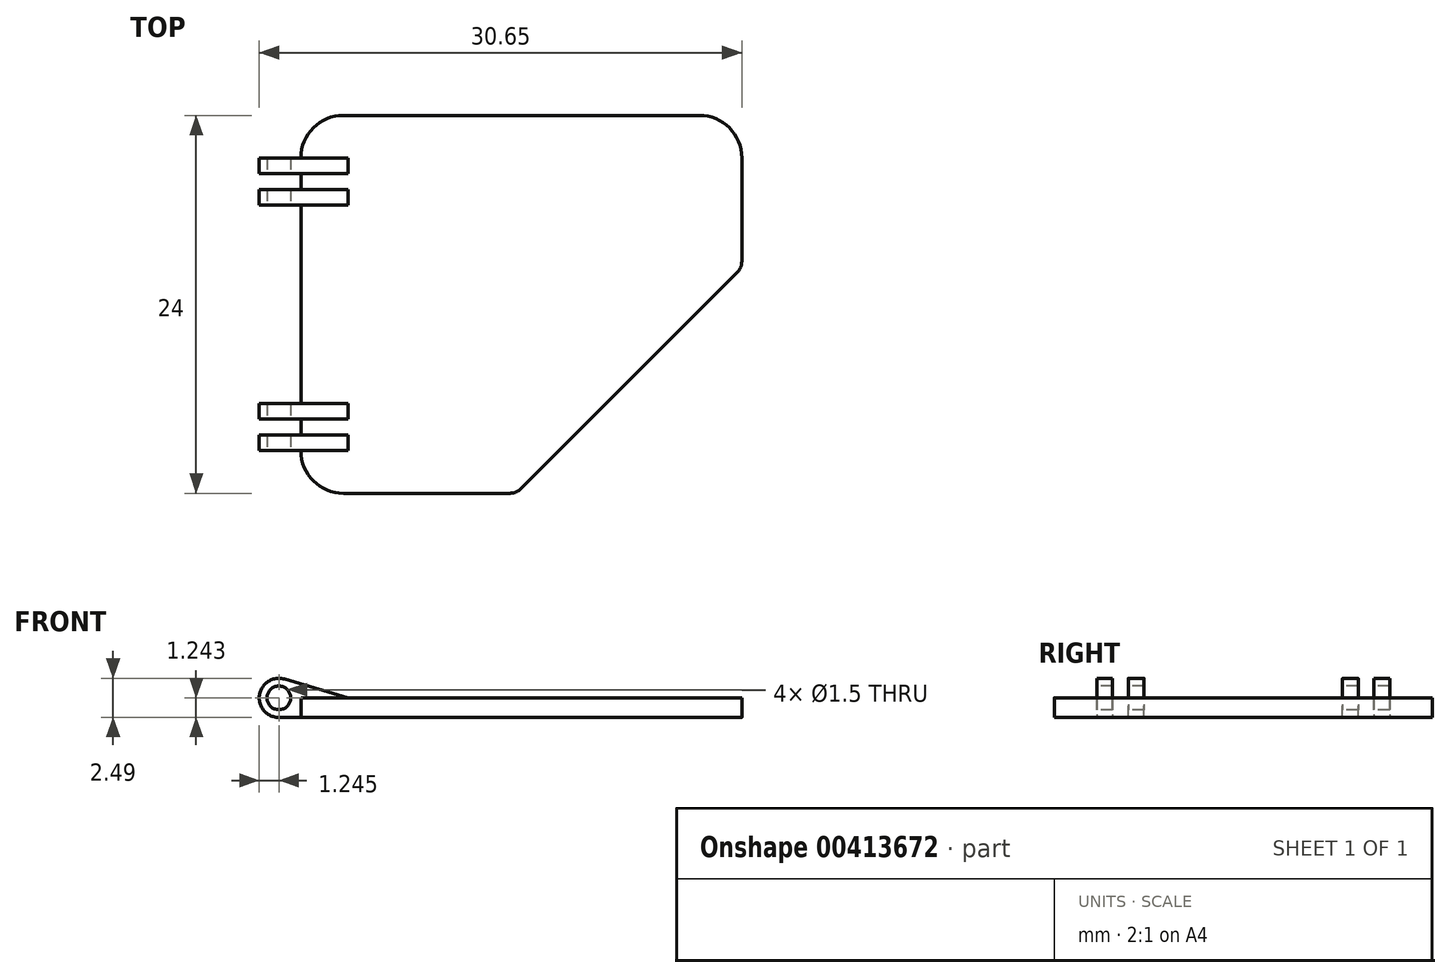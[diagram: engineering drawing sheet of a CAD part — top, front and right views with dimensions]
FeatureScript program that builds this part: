
annotation { "Feature Type Name" : "Feature", "Feature Type Description" : "" }
export const myFeature = defineFeature(function(context is Context, id is Id, definition is map)
    precondition{}
    {
        {
            var Q0;
            Q0=qCreatedBy(makeId("Top.planeOp"),FACE);
            var sketch = newSketch(context, id + "F0", { "sketchPlane" : qUnion([Q0])});
            skLineSegment(sketch, "E0", {"start": v(-10.68, 12.54) * mm, "end": v(-10.68, -6.06) * mm});
            skLineSegment(sketch, "E1", {"start": v(-7.98, -8.76) * mm, "end": v(2.6, -8.76) * mm});
            skLineSegment(sketch, "E2", {"start": v(3.3, -8.46) * mm, "end": v(17.02, 5.25) * mm});
            skLineSegment(sketch, "E3", {"start": v(17.32, 5.96) * mm, "end": v(17.32, 12.54) * mm});
            skLineSegment(sketch, "E4", {"start": v(14.62, 15.24) * mm, "end": v(-7.98, 15.24) * mm});
            skPoint(sketch, "E5.visualSharp", {"position": v(-10.68, 15.24) * mm});
            skArc(sketch, "E5.filletArc", {"start": v(-7.98, 15.24) * mm, "mid": v(-9.9, 14.45) * mm, "end": v(-10.68, 12.54) * mm});
            skPoint(sketch, "E6.visualSharp", {"position": v(-10.68, -8.76) * mm});
            skArc(sketch, "E6.filletArc", {"start": v(-10.68, -6.06) * mm, "mid": v(-9.9, -7.97) * mm, "end": v(-7.98, -8.76) * mm});
            skPoint(sketch, "E7.visualSharp", {"position": v(17.32, 15.24) * mm});
            skArc(sketch, "E7.filletArc", {"start": v(17.32, 12.54) * mm, "mid": v(16.52, 14.45) * mm, "end": v(14.62, 15.24) * mm});
            skPoint(sketch, "E8.visualSharp", {"position": v(3.02, -8.76) * mm});
            skArc(sketch, "E8.filletArc", {"start": v(2.6, -8.76) * mm, "mid": v(2.98, -8.68) * mm, "end": v(3.3, -8.46) * mm});
            skPoint(sketch, "E9.visualSharp", {"position": v(17.32, 5.54) * mm});
            skArc(sketch, "E9.filletArc", {"start": v(17.02, 5.25) * mm, "mid": v(17.24, 5.57) * mm, "end": v(17.32, 5.96) * mm});
            skSolve(sketch);
        }
        {
            var Q0;
            Q0 = qSketchRegion(id + "F0", true);
            extrude(context, id + "F1", {"entities" : qUnion([Q0]), "depth" : 1.25 * mm});
        }
        {
            var Q0;
            Q0=makeQuery(id+"F1.opExtrude","CAP_FACE",FACE,{"disambiguationData":[OSD([sQuery(id+"F0.wireOp",EDGE,"E0"),sQuery(id+"F0.wireOp",EDGE,"E1"),sQuery(id+"F0.wireOp",EDGE,"E2"),sQuery(id+"F0.wireOp",EDGE,"E3"),sQuery(id+"F0.wireOp",EDGE,"E4"),sQuery(id+"F0.wireOp",EDGE,"E5.filletArc"),sQuery(id+"F0.wireOp",EDGE,"E6.filletArc"),sQuery(id+"F0.wireOp",EDGE,"E7.filletArc"),sQuery(id+"F0.wireOp",EDGE,"E8.filletArc"),sQuery(id+"F0.wireOp",EDGE,"E9.filletArc")])],"isStart":false});
            var sketch = newSketch(context, id + "F2", { "sketchPlane" : qUnion([Q0])});
            skLineSegment(sketch, "E10", {"start": v(-10.68, 12.54) * mm, "end": v(-13.68, 12.54) * mm});
            skLineSegment(sketch, "E11", {"start": v(-13.68, 12.54) * mm, "end": v(-13.68, 11.54) * mm});
            skLineSegment(sketch, "E12", {"start": v(-13.68, 9.54) * mm, "end": v(-7.68, 9.54) * mm});
            skLineSegment(sketch, "E13", {"start": v(-7.68, 9.54) * mm, "end": v(-7.68, 10.54) * mm});
            skLineSegment(sketch, "E14", {"start": v(-7.68, 12.54) * mm, "end": v(-10.68, 12.54) * mm});
            skLineSegment(sketch, "E15", {"start": v(-10.68, -6.06) * mm, "end": v(-13.68, -6.06) * mm});
            skLineSegment(sketch, "E16", {"start": v(-13.68, -6.06) * mm, "end": v(-13.68, -5.06) * mm});
            skLineSegment(sketch, "E17", {"start": v(-13.68, -3.06) * mm, "end": v(-7.68, -3.06) * mm});
            skLineSegment(sketch, "E18", {"start": v(-7.68, -3.06) * mm, "end": v(-7.68, -4.06) * mm});
            skLineSegment(sketch, "E19", {"start": v(-7.68, -6.06) * mm, "end": v(-10.68, -6.06) * mm});
            skLineSegment(sketch, "E20.0", {"start": v(-10.68, 11.54) * mm, "end": v(-13.68, 11.54) * mm});
            skLineSegment(sketch, "E21.0", {"start": v(-7.68, 11.54) * mm, "end": v(-10.68, 11.54) * mm});
            skLineSegment(sketch, "E22.0", {"start": v(-13.68, 10.54) * mm, "end": v(-7.68, 10.54) * mm});
            skLineSegment(sketch, "E23.0", {"start": v(-13.68, -4.06) * mm, "end": v(-7.68, -4.06) * mm});
            skLineSegment(sketch, "E24.0", {"start": v(-10.68, -5.06) * mm, "end": v(-13.68, -5.06) * mm});
            skLineSegment(sketch, "E25.0", {"start": v(-7.68, -5.06) * mm, "end": v(-10.68, -5.06) * mm});
            skLineSegment(sketch, "E26.trimOffspring", {"start": v(-7.68, -5.06) * mm, "end": v(-7.68, -6.06) * mm});
            skLineSegment(sketch, "E27.trimOffspring", {"start": v(-13.68, -4.06) * mm, "end": v(-13.68, -3.06) * mm});
            skLineSegment(sketch, "E28.trimOffspring", {"start": v(-13.68, 10.54) * mm, "end": v(-13.68, 9.54) * mm});
            skLineSegment(sketch, "E29.trimOffspring", {"start": v(-7.68, 11.54) * mm, "end": v(-7.68, 12.54) * mm});
            skSolve(sketch);
        }
        {
            var Q0;
            Q0 = qSketchRegion(id + "F2", true);
            extrude(context, id + "F3", {"entities" : qUnion([Q0]), "operationType" : NewBodyOperationType.ADD, "endBound" : BoundingType.SYMMETRIC, "depth" : 5 * mm});
        }
        {
            var Q0;
            Q0=makeQuery(id+"F3.opExtrude","SWEPT_FACE",FACE,{"disambiguationData":[OSD([sQuery(id+"F2.wireOp",EDGE,"E15"),sQuery(id+"F2.wireOp",EDGE,"E19")])]});
            var sketch = newSketch(context, id + "F4", { "sketchPlane" : qUnion([Q0])});
            skLineSegment(sketch, "E30", {"start": v(-7.68, 1.25) * mm, "end": v(-7.68, 3.75) * mm});
            skLineSegment(sketch, "E31", {"start": v(-7.68, 3.75) * mm, "end": v(-13.68, 3.75) * mm});
            skLineSegment(sketch, "E32", {"start": v(-13.68, 3.75) * mm, "end": v(-13.68, -1.25) * mm});
            skLineSegment(sketch, "E33", {"start": v(-13.68, -1.25) * mm, "end": v(-7.68, -1.25) * mm});
            skLineSegment(sketch, "E34", {"start": v(-7.68, -1.25) * mm, "end": v(-7.68, 0) * mm});
            skLineSegment(sketch, "E35", {"start": v(-7.68, 0) * mm, "end": v(-10.68, 0) * mm});
            skPoint(sketch, "E36.centerSnap0", {"position": v(-10.68, 0.62) * mm});
            skLineSegment(sketch, "E37", {"start": v(-7.68, 1.25) * mm, "end": v(-10.68, 1.25) * mm});
            skLineSegment(sketch, "E38", {"start": v(-10.68, 1.25) * mm, "end": v(-10.68, 0) * mm});
            skPoint(sketch, "E39.11.internal.orphan", {"position": v(-7.68, 1.1) * mm});
            skPoint(sketch, "E40.center.orphan", {"position": v(-11.47, 0.62) * mm});
            skCircle(sketch, "E41", {"center": v(-12.08, 1.24) * mm, "radius": 0.75 * mm});
            skLineSegment(sketch, "E42", {"start": v(-10.68, 0) * mm, "end": v(-12.08, 0) * mm});
            skArc(sketch, "E43", {"start": v(-11.74, 2.44) * mm, "mid": v(-13.32, 1.42) * mm, "end": v(-12.08, 0) * mm});
            skLineSegment(sketch, "E44", {"start": v(-7.68, 1.25) * mm, "end": v(-11.74, 2.44) * mm});
            skSolve(sketch);
        }
        {
            var Q0;
            Q0=makeQuery(id+"F4.imprint","IMPRINT",FACE,{"disambiguationData":[TD([[makeQuery(id+"F4.imprint","IMPRINT",EDGE,{"derivedFrom":sQuery(id+"F4.wireOp",EDGE,"E30")}),-1.0]])]});
            var Q1;
            Q1=makeQuery(id+"F4.imprint","IMPRINT",FACE,{"disambiguationData":[TD([[makeQuery(id+"F4.imprint","IMPRINT",EDGE,{"derivedFrom":sQuery(id+"F4.wireOp",EDGE,"P1NodEf6-Nj30-rcLm-JhfE-Ix62rEcOrYL7")}),1.0]])]});
            var Q2;
            Q2=makeQuery(id+"F4.imprint","IMPRINT",FACE,{"disambiguationData":[TD([[makeQuery(id+"F4.imprint","IMPRINT",EDGE,{"derivedFrom":sQuery(id+"F4.wireOp",EDGE,"E41")}),1.0]])]});
            extrude(context, id + "F5", {"entities" : qUnion([Q0, Q1, Q2]), "operationType" : NewBodyOperationType.REMOVE, "oppositeDirection" : true, "depth" : 75 * mm});
        }
    });
